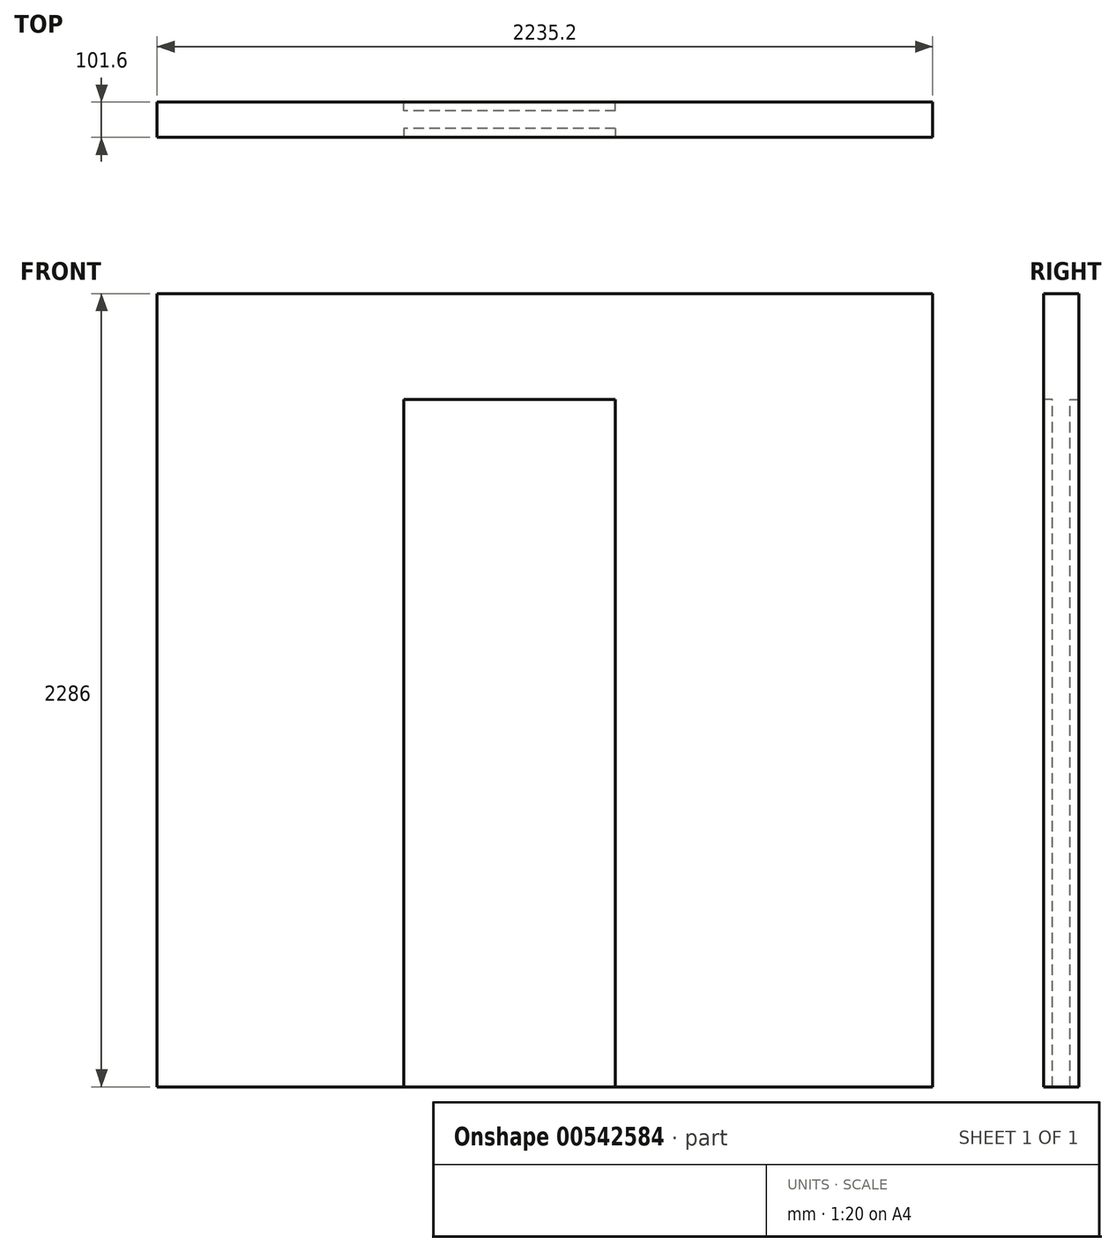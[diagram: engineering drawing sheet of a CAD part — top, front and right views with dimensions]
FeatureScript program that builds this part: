
annotation { "Feature Type Name" : "Feature", "Feature Type Description" : "" }
export const myFeature = defineFeature(function(context is Context, id is Id, definition is map)
    precondition{}
    {
        {
            var Q0;
            Q0=qCreatedBy(makeId("Front.planeOp"),FACE);
            var sketch = newSketch(context, id + "F0", { "sketchPlane" : qUnion([Q0])});
            skLineSegment(sketch, "E0.bottom", {"start": v(0, 0) * mm, "end": v(-2235.2, 0) * mm});
            skLineSegment(sketch, "E0.top", {"start": v(0, 2286) * mm, "end": v(-2235.2, 2286) * mm});
            skLineSegment(sketch, "E0.left", {"start": v(0, 0) * mm, "end": v(0, 2286) * mm});
            skLineSegment(sketch, "E0.right", {"start": v(-2235.2, 0) * mm, "end": v(-2235.2, 2286) * mm});
            skSolve(sketch);
        }
        {
            var Q0;
            Q0=makeQuery(id+"F0.imprint","IMPRINT",FACE,{"disambiguationData":[TD([[makeQuery(id+"F0.imprint","IMPRINT",EDGE,{"derivedFrom":sQuery(id+"F0.wireOp",EDGE,"E0.bottom")}),-1.0]])]});
            extrude(context, id + "F1", {"entities" : qUnion([Q0]), "depth" : 101.6 * mm, "offsetDistance" : 25.4 * mm});
        }
        {
            var Q0;
            Q0=makeQuery(id+"F1.opExtrude","CAP_FACE",FACE,{"disambiguationData":[OSD([sQuery(id+"F0.wireOp",EDGE,"E0.bottom"),sQuery(id+"F0.wireOp",EDGE,"E0.top"),sQuery(id+"F0.wireOp",EDGE,"E0.left"),sQuery(id+"F0.wireOp",EDGE,"E0.right")])],"isStart":false});
            var sketch = newSketch(context, id + "F2", { "sketchPlane" : qUnion([Q0])});
            skLineSegment(sketch, "E1.bottom", {"start": v(-1524, 0) * mm, "end": v(-914.4, 0) * mm});
            skLineSegment(sketch, "E1.top", {"start": v(-1524, 1981.2) * mm, "end": v(-914.4, 1981.2) * mm});
            skLineSegment(sketch, "E1.left", {"start": v(-1524, 0) * mm, "end": v(-1524, 1981.2) * mm});
            skLineSegment(sketch, "E1.right", {"start": v(-914.4, 0) * mm, "end": v(-914.4, 1981.2) * mm});
            skSolve(sketch);
        }
        {
            var Q0;
            Q0=makeQuery(id+"F2.imprint","IMPRINT",FACE,{"disambiguationData":[TD([[makeQuery(id+"F2.imprint","IMPRINT",EDGE,{"derivedFrom":sQuery(id+"F2.wireOp",EDGE,"E1.bottom")}),-1.0]])]});
            extrude(context, id + "F3", {"entities" : qUnion([Q0]), "operationType" : NewBodyOperationType.REMOVE, "oppositeDirection" : true, "depth" : 25.4 * mm, "offsetDistance" : 25.4 * mm});
        }
        {
            var Q0;
            Q0=makeQuery(id+"F1.opExtrude","CAP_FACE",FACE,{"disambiguationData":[OSD([sQuery(id+"F0.wireOp",EDGE,"E0.bottom"),sQuery(id+"F0.wireOp",EDGE,"E0.top"),sQuery(id+"F0.wireOp",EDGE,"E0.left"),sQuery(id+"F0.wireOp",EDGE,"E0.right")])],"isStart":true});
            var sketch = newSketch(context, id + "F4", { "sketchPlane" : qUnion([Q0])});
            skLineSegment(sketch, "E2.bottom", {"start": v(914.4, 0) * mm, "end": v(1524, 0) * mm});
            skLineSegment(sketch, "E2.top", {"start": v(914.4, 1981.2) * mm, "end": v(1524, 1981.2) * mm});
            skLineSegment(sketch, "E2.left", {"start": v(914.4, 0) * mm, "end": v(914.4, 1981.2) * mm});
            skLineSegment(sketch, "E2.right", {"start": v(1524, 0) * mm, "end": v(1524, 1981.2) * mm});
            skSolve(sketch);
        }
        {
            var Q0;
            Q0=makeQuery(id+"F4.imprint","IMPRINT",FACE,{"disambiguationData":[TD([[makeQuery(id+"F4.imprint","IMPRINT",EDGE,{"derivedFrom":sQuery(id+"F4.wireOp",EDGE,"E2.bottom")}),1.0]])]});
            extrude(context, id + "F5", {"entities" : qUnion([Q0]), "operationType" : NewBodyOperationType.REMOVE, "oppositeDirection" : true, "depth" : 25.4 * mm, "offsetDistance" : 25.4 * mm});
        }
    });
